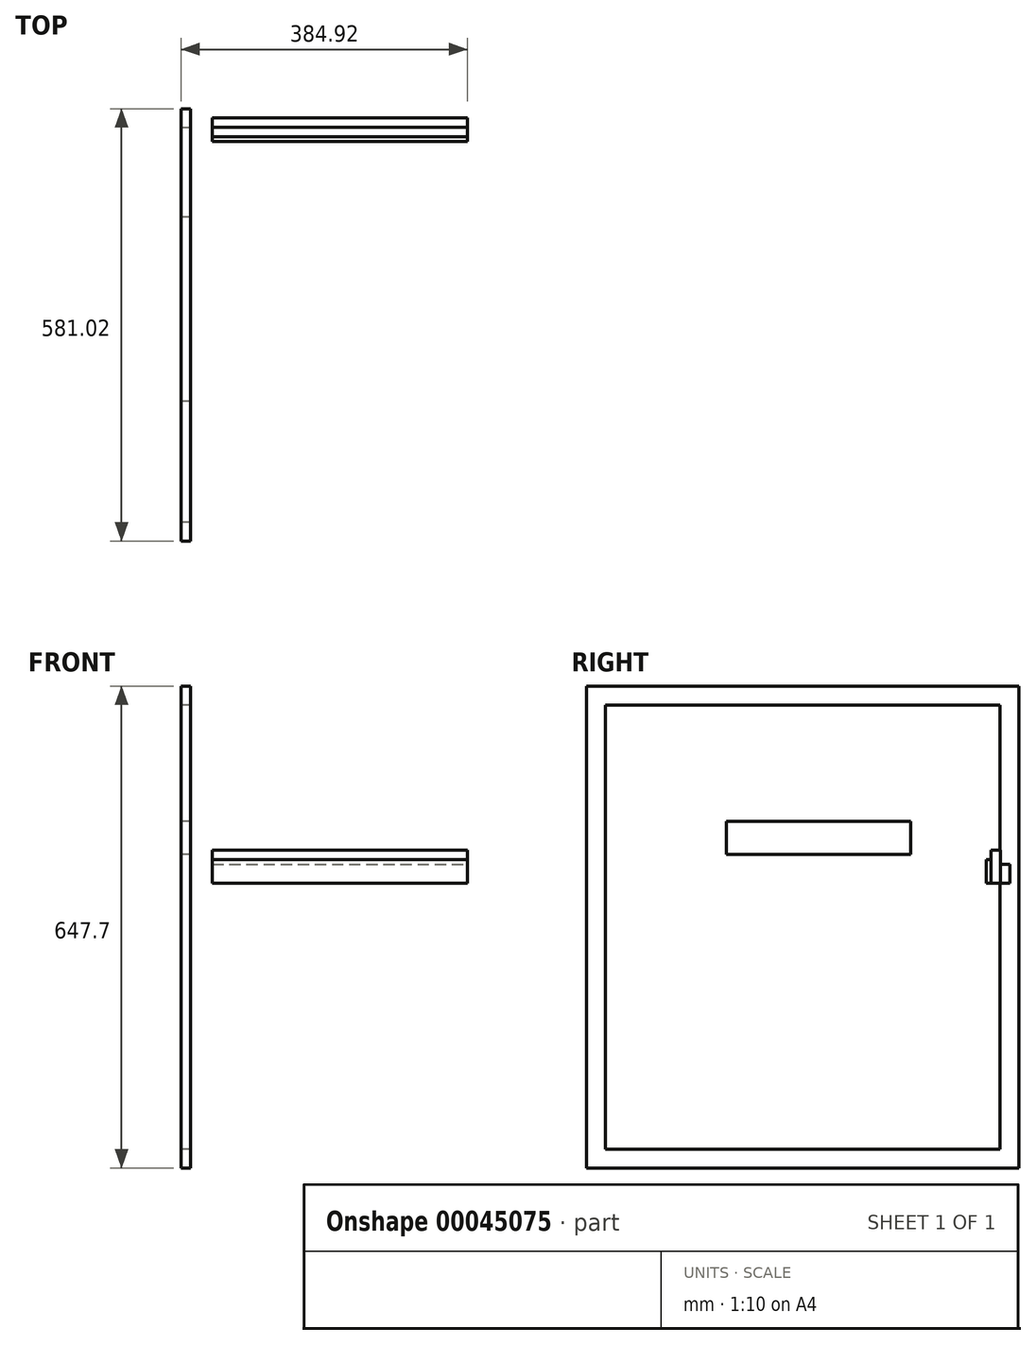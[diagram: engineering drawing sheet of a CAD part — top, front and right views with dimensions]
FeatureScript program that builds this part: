
annotation { "Feature Type Name" : "Feature", "Feature Type Description" : "" }
export const myFeature = defineFeature(function(context is Context, id is Id, definition is map)
    precondition{}
    {
        {
            var Q0;
            Q0=qCreatedBy(makeId("Right.planeOp"),FACE);
            var sketch = newSketch(context, id + "F0", { "sketchPlane" : qUnion([Q0])});
            skLineSegment(sketch, "E0.bottom", {"start": v(-297.23, 264.94) * mm, "end": v(283.8, 264.94) * mm});
            skLineSegment(sketch, "E0.top", {"start": v(-297.23, -382.76) * mm, "end": v(283.8, -382.76) * mm});
            skLineSegment(sketch, "E0.left", {"start": v(-297.23, 264.94) * mm, "end": v(-297.23, -382.76) * mm});
            skLineSegment(sketch, "E0.right", {"start": v(283.8, 264.94) * mm, "end": v(283.8, -382.76) * mm});
            skLineSegment(sketch, "E1.0", {"start": v(258.4, 239.54) * mm, "end": v(258.4, -357.36) * mm});
            skLineSegment(sketch, "E1.1", {"start": v(-271.83, 239.54) * mm, "end": v(258.4, 239.54) * mm});
            skLineSegment(sketch, "E2.trimOffspring", {"start": v(-271.83, 239.54) * mm, "end": v(-271.83, -357.36) * mm});
            skLineSegment(sketch, "E3", {"start": v(-271.83, -357.36) * mm, "end": v(258.4, -357.36) * mm});
            skSolve(sketch);
        }
        {
            var Q0;
            Q0=makeQuery(id+"F0.imprint","IMPRINT",FACE,{"disambiguationData":[TD([[makeQuery(id+"F0.imprint","IMPRINT",EDGE,{"derivedFrom":sQuery(id+"F0.wireOp",EDGE,"E0.bottom")}),-1.0]])]});
            extrude(context, id + "F1", {"entities" : qUnion([Q0]), "depth" : 12.7 * mm});
        }
        {
            var Q0;
            Q0=qCreatedBy(makeId("Top.planeOp"),FACE);
            var sketch = newSketch(context, id + "F2", { "sketchPlane" : qUnion([Q0])});
            skLineSegment(sketch, "E4.bottom", {"start": v(42.02, 271.46) * mm, "end": v(384.92, 271.46) * mm});
            skLineSegment(sketch, "E4.top", {"start": v(42.02, 258.76) * mm, "end": v(384.92, 258.76) * mm});
            skLineSegment(sketch, "E4.left", {"start": v(42.02, 271.46) * mm, "end": v(42.02, 258.76) * mm});
            skLineSegment(sketch, "E4.right", {"start": v(384.92, 271.46) * mm, "end": v(384.92, 258.76) * mm});
            skSolve(sketch);
        }
        {
            var Q0;
            Q0=makeQuery(id+"F2.imprint","IMPRINT",FACE,{"disambiguationData":[TD([[makeQuery(id+"F2.imprint","IMPRINT",EDGE,{"derivedFrom":sQuery(id+"F2.wireOp",EDGE,"E4.bottom")}),-1.0]])]});
            extrude(context, id + "F3", {"entities" : qUnion([Q0]), "depth" : 25.4 * mm});
        }
        {
            var Q0;
            Q0=makeQuery(id+"F3.opExtrude","SWEPT_FACE",FACE,{"disambiguationData":[OSD([sQuery(id+"F2.wireOp",EDGE,"E4.top")])]});
            var sketch = newSketch(context, id + "F4", { "sketchPlane" : qUnion([Q0])});
            skPoint(sketch, "E5.oppositeSnap0", {"position": v(384.92, 12.7) * mm});
            skLineSegment(sketch, "E5.bottom", {"start": v(42.02, 0) * mm, "end": v(384.92, 0) * mm});
            skLineSegment(sketch, "E5.top", {"start": v(42.02, 44.45) * mm, "end": v(384.92, 44.45) * mm});
            skLineSegment(sketch, "E5.left", {"start": v(42.02, 0) * mm, "end": v(42.02, 44.45) * mm});
            skLineSegment(sketch, "E5.right", {"start": v(384.92, 0) * mm, "end": v(384.92, 44.45) * mm});
            skSolve(sketch);
        }
        {
            var Q0;
            {var subQ2=sQuery(id+"F4.wireOp",EDGE,"E5.bottom");Q0=makeQuery(id+"F4.imprint","IMPRINT",FACE,{"disambiguationData":[TD([[makeQuery(id+"F4.imprint","IMPRINT",EDGE,{"derivedFrom":subQ2}),1.0]])]});}
            var Q1;
            {var subQ2=sQuery(id+"F4.wireOp",EDGE,"E5.top");Q1=makeQuery(id+"F4.imprint","IMPRINT",FACE,{"disambiguationData":[TD([[makeQuery(id+"F4.imprint","IMPRINT",EDGE,{"derivedFrom":subQ2}),-1.0]])]});}
            extrude(context, id + "F5", {"entities" : qUnion([Q0, Q1]), "depth" : 12.7 * mm});
        }
        {
            var Q0;
            Q0=makeQuery(id+"F5.opExtrude","CAP_FACE",FACE,{"disambiguationData":[OSD([sQuery(id+"F4.wireOp",EDGE,"E5.bottom"),sQuery(id+"F4.wireOp",EDGE,"E5.top"),sQuery(id+"F4.wireOp",EDGE,"E5.left"),sQuery(id+"F4.wireOp",EDGE,"E5.right")])],"isStart":false});
            var sketch = newSketch(context, id + "F6", { "sketchPlane" : qUnion([Q0])});
            skLineSegment(sketch, "E6.bottom", {"start": v(42.02, 0) * mm, "end": v(384.92, 0) * mm});
            skLineSegment(sketch, "E6.top", {"start": v(42.02, 31.75) * mm, "end": v(384.92, 31.75) * mm});
            skLineSegment(sketch, "E6.left", {"start": v(42.02, 0) * mm, "end": v(42.02, 31.75) * mm});
            skLineSegment(sketch, "E6.right", {"start": v(384.92, 0) * mm, "end": v(384.92, 31.75) * mm});
            skSolve(sketch);
        }
        {
            var Q0;
            Q0=makeQuery(id+"F6.imprint","IMPRINT",FACE,{"disambiguationData":[TD([[makeQuery(id+"F6.imprint","IMPRINT",EDGE,{"derivedFrom":sQuery(id+"F6.wireOp",EDGE,"E6.bottom")}),1.0]])]});
            extrude(context, id + "F7", {"entities" : qUnion([Q0]), "depth" : 6.35 * mm});
        }
        {
            var Q0;
            Q0=qCreatedBy(makeId("Right.planeOp"),FACE);
            var sketch = newSketch(context, id + "F8", { "sketchPlane" : qUnion([Q0])});
            skLineSegment(sketch, "E7.bottom", {"start": v(-109.49, 38.65) * mm, "end": v(138.16, 38.65) * mm});
            skLineSegment(sketch, "E7.top", {"start": v(-109.49, 83.1) * mm, "end": v(138.16, 83.1) * mm});
            skLineSegment(sketch, "E7.left", {"start": v(-109.49, 38.65) * mm, "end": v(-109.49, 83.1) * mm});
            skLineSegment(sketch, "E7.right", {"start": v(138.16, 38.65) * mm, "end": v(138.16, 83.1) * mm});
            skSolve(sketch);
        }
        {
            var Q0;
            Q0=makeQuery(id+"F8.imprint","IMPRINT",FACE,{"disambiguationData":[TD([[makeQuery(id+"F8.imprint","IMPRINT",EDGE,{"derivedFrom":sQuery(id+"F8.wireOp",EDGE,"E7.bottom")}),1.0]])]});
            extrude(context, id + "F9", {"entities" : qUnion([Q0]), "depth" : 12.7 * mm});
        }
    });
